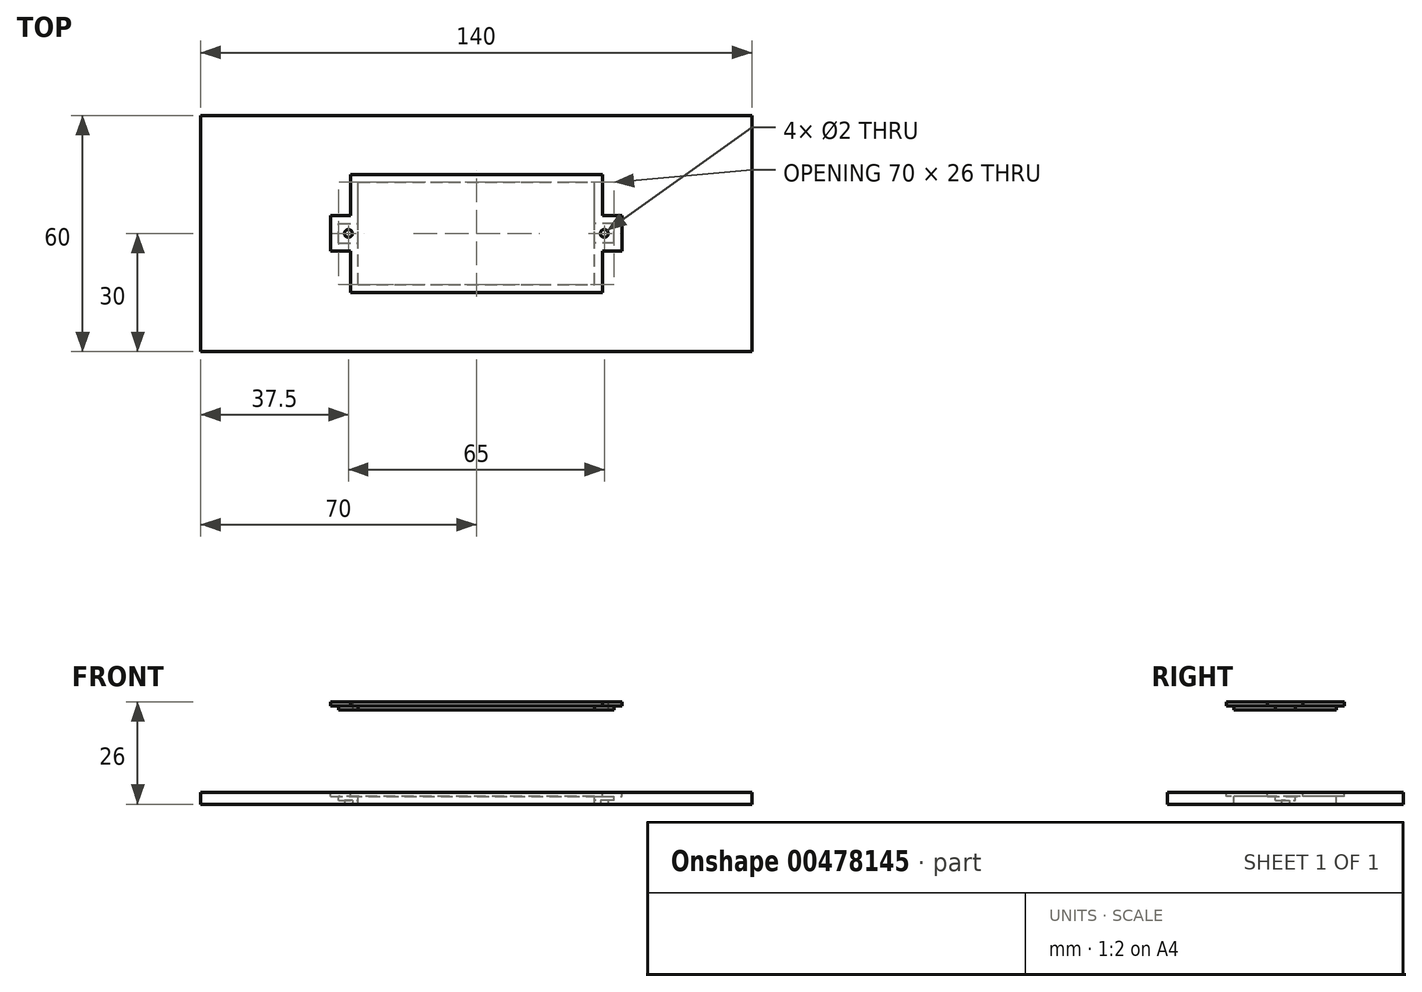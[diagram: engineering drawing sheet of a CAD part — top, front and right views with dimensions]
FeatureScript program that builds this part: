
annotation { "Feature Type Name" : "Feature", "Feature Type Description" : "" }
export const myFeature = defineFeature(function(context is Context, id is Id, definition is map)
    precondition{}
    {
        {
            var Q0;
            Q0=qCreatedBy(makeId("Top.planeOp"),FACE);
            var sketch = newSketch(context, id + "F0", { "sketchPlane" : qUnion([Q0])});
            skLineSegment(sketch, "E0.bottom", {"start": v(70, -30) * mm, "end": v(-70, -30) * mm});
            skLineSegment(sketch, "E0.top", {"start": v(70, 30) * mm, "end": v(-70, 30) * mm});
            skLineSegment(sketch, "E0.left", {"start": v(70, -30) * mm, "end": v(70, 30) * mm});
            skLineSegment(sketch, "E0.right", {"start": v(-70, -30) * mm, "end": v(-70, 30) * mm});
            skPoint(sketch, "E0.middle", {"position": v(0, 0) * mm});
            skSolve(sketch);
        }
        {
            var Q0;
            Q0 = qSketchRegion(id + "F0", true);
            extrude(context, id + "F1", {"entities" : qUnion([Q0]), "depth" : 3 * mm});
        }
        {
            var Q0;
            Q0=makeQuery(id+"F1.opExtrude","CAP_FACE",FACE,{"disambiguationData":[OSD([sQuery(id+"F0.wireOp",EDGE,"E0.bottom"),sQuery(id+"F0.wireOp",EDGE,"E0.top"),sQuery(id+"F0.wireOp",EDGE,"E0.left"),sQuery(id+"F0.wireOp",EDGE,"E0.right")])],"isStart":false});
            var sketch = newSketch(context, id + "F2", { "sketchPlane" : qUnion([Q0])});
            skLineSegment(sketch, "E1.bottom", {"start": v(-30, -13) * mm, "end": v(30, -13) * mm});
            skLineSegment(sketch, "E1.top", {"start": v(-30, 13) * mm, "end": v(30, 13) * mm});
            skLineSegment(sketch, "E1.left", {"start": v(-30, -13) * mm, "end": v(-30, -2.5) * mm});
            skLineSegment(sketch, "E1.right", {"start": v(30, -13) * mm, "end": v(30, -2.5) * mm});
            skPoint(sketch, "E1.middle", {"position": v(0, 0) * mm});
            skLineSegment(sketch, "E2.bottom", {"start": v(-35, -2.5) * mm, "end": v(-30, -2.5) * mm});
            skLineSegment(sketch, "E2.top", {"start": v(-35, 2.5) * mm, "end": v(-30, 2.5) * mm});
            skLineSegment(sketch, "E2.left", {"start": v(-35, -2.5) * mm, "end": v(-35, 2.5) * mm});
            skPoint(sketch, "E2.middle", {"position": v(-30, 0) * mm});
            skLineSegment(sketch, "E3.bottom", {"start": v(35, -2.5) * mm, "end": v(30, -2.5) * mm});
            skLineSegment(sketch, "E3.top", {"start": v(35, 2.5) * mm, "end": v(30, 2.5) * mm});
            skLineSegment(sketch, "E3.left", {"start": v(35, -2.5) * mm, "end": v(35, 2.5) * mm});
            skPoint(sketch, "E3.middle", {"position": v(30, 0) * mm});
            skPoint(sketch, "E2.right.end.orphan", {"position": v(-25, 2.5) * mm});
            skPoint(sketch, "E4.orphan", {"position": v(-25, -2.5) * mm});
            skLineSegment(sketch, "E5.trimOffspring", {"start": v(-30, 2.5) * mm, "end": v(-30, 13) * mm});
            skPoint(sketch, "E3.right.start.orphan", {"position": v(25, -2.5) * mm});
            skPoint(sketch, "E6.orphan", {"position": v(25, 2.5) * mm});
            skLineSegment(sketch, "E7.trimOffspring", {"start": v(30, 2.5) * mm, "end": v(30, 13) * mm});
            skSolve(sketch);
        }
        {
            var Q0;
            Q0=makeQuery(id+"F2.imprint","IMPRINT",FACE,{"disambiguationData":[TD([[makeQuery(id+"F2.imprint","IMPRINT",EDGE,{"derivedFrom":sQuery(id+"F2.wireOp",EDGE,"E1.bottom")}),-1.0]])]});
            var sketch = newSketch(context, id + "F3", { "sketchPlane" : qUnion([Q0])});
            skPoint(sketch, "E8.middle", {"position": v(0, 0) * mm});
            skPoint(sketch, "E9.middle", {"position": v(-30, 0) * mm});
            skPoint(sketch, "E10.middle", {"position": v(30, 0) * mm});
            skPoint(sketch, "E9.right.start.orphan", {"position": v(-25, -2.5) * mm});
            skPoint(sketch, "E11.orphan", {"position": v(-25, 2.5) * mm});
            skPoint(sketch, "E12.orphan", {"position": v(25, 2.5) * mm});
            skPoint(sketch, "E13.orphan", {"position": v(25, -2.5) * mm});
            skLineSegment(sketch, "E14.0", {"start": v(-32, 15) * mm, "end": v(-32, 4.5) * mm});
            skLineSegment(sketch, "E14.1", {"start": v(32, -4.5) * mm, "end": v(37, -4.5) * mm});
            skLineSegment(sketch, "E14.2", {"start": v(37, -4.5) * mm, "end": v(37, 4.5) * mm});
            skLineSegment(sketch, "E14.3", {"start": v(32, 4.5) * mm, "end": v(37, 4.5) * mm});
            skLineSegment(sketch, "E14.4", {"start": v(32, 15) * mm, "end": v(32, 4.5) * mm});
            skLineSegment(sketch, "E14.5", {"start": v(32, -4.5) * mm, "end": v(32, -15) * mm});
            skLineSegment(sketch, "E14.6", {"start": v(-32, 15) * mm, "end": v(32, 15) * mm});
            skLineSegment(sketch, "E14.7", {"start": v(-32, -15) * mm, "end": v(32, -15) * mm});
            skLineSegment(sketch, "E14.8", {"start": v(-32, -4.5) * mm, "end": v(-32, -15) * mm});
            skLineSegment(sketch, "E14.9", {"start": v(-37, -4.5) * mm, "end": v(-32, -4.5) * mm});
            skLineSegment(sketch, "E14.10", {"start": v(-37, -4.5) * mm, "end": v(-37, 4.5) * mm});
            skLineSegment(sketch, "E14.11", {"start": v(-37, 4.5) * mm, "end": v(-32, 4.5) * mm});
            skSolve(sketch);
        }
        {
            var Q0;
            Q0 = qSketchRegion(id + "F2", true);
            extrude(context, id + "F4", {"entities" : qUnion([Q0]), "operationType" : NewBodyOperationType.REMOVE, "oppositeDirection" : true, "depth" : 2 * mm});
        }
        {
            var Q0;
            Q0 = qSketchRegion(id + "F3", true);
            extrude(context, id + "F5", {"entities" : qUnion([Q0]), "operationType" : NewBodyOperationType.REMOVE, "oppositeDirection" : true, "depth" : 1 * mm});
        }
        {
            var Q0;
            Q0=makeQuery(id+"F2.imprint","IMPRINT",FACE,{"disambiguationData":[TD([[makeQuery(id+"F2.imprint","IMPRINT",EDGE,{"derivedFrom":sQuery(id+"F2.wireOp",EDGE,"E1.bottom")}),1.0]])]});
            var sketch = newSketch(context, id + "F6", { "sketchPlane" : qUnion([Q0])});
            skLineSegment(sketch, "E15.bottom", {"start": v(30, -13) * mm, "end": v(-30, -13) * mm});
            skLineSegment(sketch, "E15.top", {"start": v(30, 13) * mm, "end": v(-30, 13) * mm});
            skLineSegment(sketch, "E15.left", {"start": v(30, -13) * mm, "end": v(30, 13) * mm});
            skLineSegment(sketch, "E15.right", {"start": v(-30, -13) * mm, "end": v(-30, 13) * mm});
            skPoint(sketch, "E15.middle", {"position": v(0, 0) * mm});
            skSolve(sketch);
        }
        {
            var Q0;
            Q0 = qSketchRegion(id + "F6", true);
            extrude(context, id + "F7", {"entities" : qUnion([Q0]), "operationType" : NewBodyOperationType.REMOVE, "oppositeDirection" : true, "depth" : 25 * mm});
        }
        {
            var Q0;
            Q0=qCreatedBy(makeId("Top.planeOp"),FACE);
            cPlane(context, id + "F8", {"entities" : qUnion([Q0]), "cplaneType" : CPlaneType.OFFSET, "offset" : 25 * mm, "width" : 150 * mm, "height" : 150 * mm});
        }
        {
            var Q0;
            Q0=qCreatedBy(id+"F8.planeOp",FACE);
            var sketch = newSketch(context, id + "F9", { "sketchPlane" : qUnion([Q0])});
            skLineSegment(sketch, "E16.bottom", {"start": v(-32, 15) * mm, "end": v(32, 15) * mm});
            skLineSegment(sketch, "E16.top", {"start": v(-32, -15) * mm, "end": v(32, -15) * mm});
            skLineSegment(sketch, "E16.left", {"start": v(-32, 15) * mm, "end": v(-32, 4.5) * mm});
            skLineSegment(sketch, "E16.right", {"start": v(32, 15) * mm, "end": v(32, 4.5) * mm});
            skPoint(sketch, "E16.middle", {"position": v(0, 0) * mm});
            skLineSegment(sketch, "E17.bottom", {"start": v(-37, -4.5) * mm, "end": v(-32, -4.5) * mm});
            skLineSegment(sketch, "E17.top", {"start": v(-37, 4.5) * mm, "end": v(-32, 4.5) * mm});
            skLineSegment(sketch, "E17.left", {"start": v(-37, -4.5) * mm, "end": v(-37, 4.5) * mm});
            skPoint(sketch, "E17.middle", {"position": v(-32, 0) * mm});
            skPoint(sketch, "E17.right.start.orphan", {"position": v(-27, -4.5) * mm});
            skPoint(sketch, "E18.orphan", {"position": v(-27, 4.5) * mm});
            skLineSegment(sketch, "E19.trimOffspring", {"start": v(-32, -4.5) * mm, "end": v(-32, -15) * mm});
            skLineSegment(sketch, "E20.bottom", {"start": v(37, -4.5) * mm, "end": v(32, -4.5) * mm});
            skLineSegment(sketch, "E20.top", {"start": v(37, 4.5) * mm, "end": v(32, 4.5) * mm});
            skLineSegment(sketch, "E20.left", {"start": v(37, -4.5) * mm, "end": v(37, 4.5) * mm});
            skPoint(sketch, "E20.middle", {"position": v(32, 0) * mm});
            skPoint(sketch, "E20.right.end.orphan", {"position": v(27, 4.5) * mm});
            skPoint(sketch, "E21.orphan", {"position": v(27, -4.5) * mm});
            skLineSegment(sketch, "E22.trimOffspring", {"start": v(32, -4.5) * mm, "end": v(32, -15) * mm});
            skSolve(sketch);
        }
        {
            var Q0;
            Q0=qCreatedBy(id+"F8.planeOp",FACE);
            var sketch = newSketch(context, id + "F10", { "sketchPlane" : qUnion([Q0])});
            skLineSegment(sketch, "E23.bottom", {"start": v(-30, -13) * mm, "end": v(30, -13) * mm});
            skLineSegment(sketch, "E23.top", {"start": v(-30, 13) * mm, "end": v(30, 13) * mm});
            skLineSegment(sketch, "E23.left", {"start": v(-30, -13) * mm, "end": v(-30, -2.5) * mm});
            skLineSegment(sketch, "E23.right", {"start": v(30, -13) * mm, "end": v(30, -2.5) * mm});
            skPoint(sketch, "E23.middle", {"position": v(0, 0) * mm});
            skLineSegment(sketch, "E24.bottom", {"start": v(35, -2.5) * mm, "end": v(30, -2.5) * mm});
            skLineSegment(sketch, "E24.top", {"start": v(35, 2.5) * mm, "end": v(30, 2.5) * mm});
            skLineSegment(sketch, "E24.left", {"start": v(35, -2.5) * mm, "end": v(35, 2.5) * mm});
            skPoint(sketch, "E24.middle", {"position": v(30, 0) * mm});
            skLineSegment(sketch, "E25.bottom", {"start": v(-35, -2.5) * mm, "end": v(-30, -2.5) * mm});
            skLineSegment(sketch, "E25.top", {"start": v(-35, 2.5) * mm, "end": v(-30, 2.5) * mm});
            skLineSegment(sketch, "E25.left", {"start": v(-35, -2.5) * mm, "end": v(-35, 2.5) * mm});
            skPoint(sketch, "E25.middle", {"position": v(-30, 0) * mm});
            skPoint(sketch, "E25.right.start.orphan", {"position": v(-25, -2.5) * mm});
            skPoint(sketch, "E26.orphan", {"position": v(-25, 2.5) * mm});
            skLineSegment(sketch, "E27.trimOffspring", {"start": v(-30, 2.5) * mm, "end": v(-30, 13) * mm});
            skPoint(sketch, "E24.right.end.orphan", {"position": v(25, 2.5) * mm});
            skPoint(sketch, "E24.right.start.orphan", {"position": v(25, -2.5) * mm});
            skLineSegment(sketch, "E28.trimOffspring", {"start": v(30, 2.5) * mm, "end": v(30, 13) * mm});
            skSolve(sketch);
        }
        {
            var Q0;
            Q0 = qSketchRegion(id + "F10", true);
            extrude(context, id + "F11", {"entities" : qUnion([Q0]), "oppositeDirection" : true, "depth" : 1 * mm});
        }
        {
            var Q0;
            Q0 = qSketchRegion(id + "F9", true);
            extrude(context, id + "F12", {"entities" : qUnion([Q0]), "operationType" : NewBodyOperationType.ADD, "depth" : 1 * mm});
        }
        {
            var Q0;
            Q0=makeQuery(id+"F1.opExtrude","CAP_FACE",FACE,{"disambiguationData":[OSD([sQuery(id+"F0.wireOp",EDGE,"E0.bottom"),sQuery(id+"F0.wireOp",EDGE,"E0.top"),sQuery(id+"F0.wireOp",EDGE,"E0.left"),sQuery(id+"F0.wireOp",EDGE,"E0.right")])],"isStart":true});
            var sketch = newSketch(context, id + "F13", { "sketchPlane" : qUnion([Q0])});
            skLineSegment(sketch, "E29.bottom", {"start": v(-35, -2.5) * mm, "end": v(-25, -2.5) * mm, "construction": true});
            skLineSegment(sketch, "E29.top", {"start": v(-35, 2.5) * mm, "end": v(-25, 2.5) * mm, "construction": true});
            skLineSegment(sketch, "E29.left", {"start": v(-35, -2.5) * mm, "end": v(-35, 2.5) * mm, "construction": true});
            skLineSegment(sketch, "E29.right", {"start": v(-25, -2.5) * mm, "end": v(-25, 2.5) * mm, "construction": true});
            skPoint(sketch, "E29.middle", {"position": v(-30, 0) * mm});
            skLineSegment(sketch, "E30.bottom", {"start": v(35, -2.5) * mm, "end": v(25, -2.5) * mm, "construction": true});
            skLineSegment(sketch, "E30.top", {"start": v(35, 2.5) * mm, "end": v(25, 2.5) * mm, "construction": true});
            skLineSegment(sketch, "E30.left", {"start": v(35, -2.5) * mm, "end": v(35, 2.5) * mm, "construction": true});
            skLineSegment(sketch, "E30.right", {"start": v(25, -2.5) * mm, "end": v(25, 2.5) * mm, "construction": true});
            skPoint(sketch, "E30.middle", {"position": v(30, 0) * mm});
            skLineSegment(sketch, "E31", {"start": v(30, 2.5) * mm, "end": v(30, -2.5) * mm, "construction": true});
            skLineSegment(sketch, "E32", {"start": v(-30, 2.5) * mm, "end": v(-30, -2.5) * mm, "construction": true});
            skLineSegment(sketch, "E33", {"start": v(-30, 0) * mm, "end": v(-25, 0) * mm, "construction": true});
            skLineSegment(sketch, "E34", {"start": v(25, 0) * mm, "end": v(30, 0) * mm, "construction": true});
            skCircle(sketch, "E35", {"center": v(-32.5, 0) * mm, "radius": 1 * mm});
            skCircle(sketch, "E36", {"center": v(32.5, 0) * mm, "radius": 1 * mm});
            skSolve(sketch);
        }
        {
            var Q0;
            Q0 = qSketchRegion(id + "F13", true);
            extrude(context, id + "F14", {"entities" : qUnion([Q0]), "operationType" : NewBodyOperationType.REMOVE, "oppositeDirection" : true, "depth" : 43 * mm});
        }
    });
